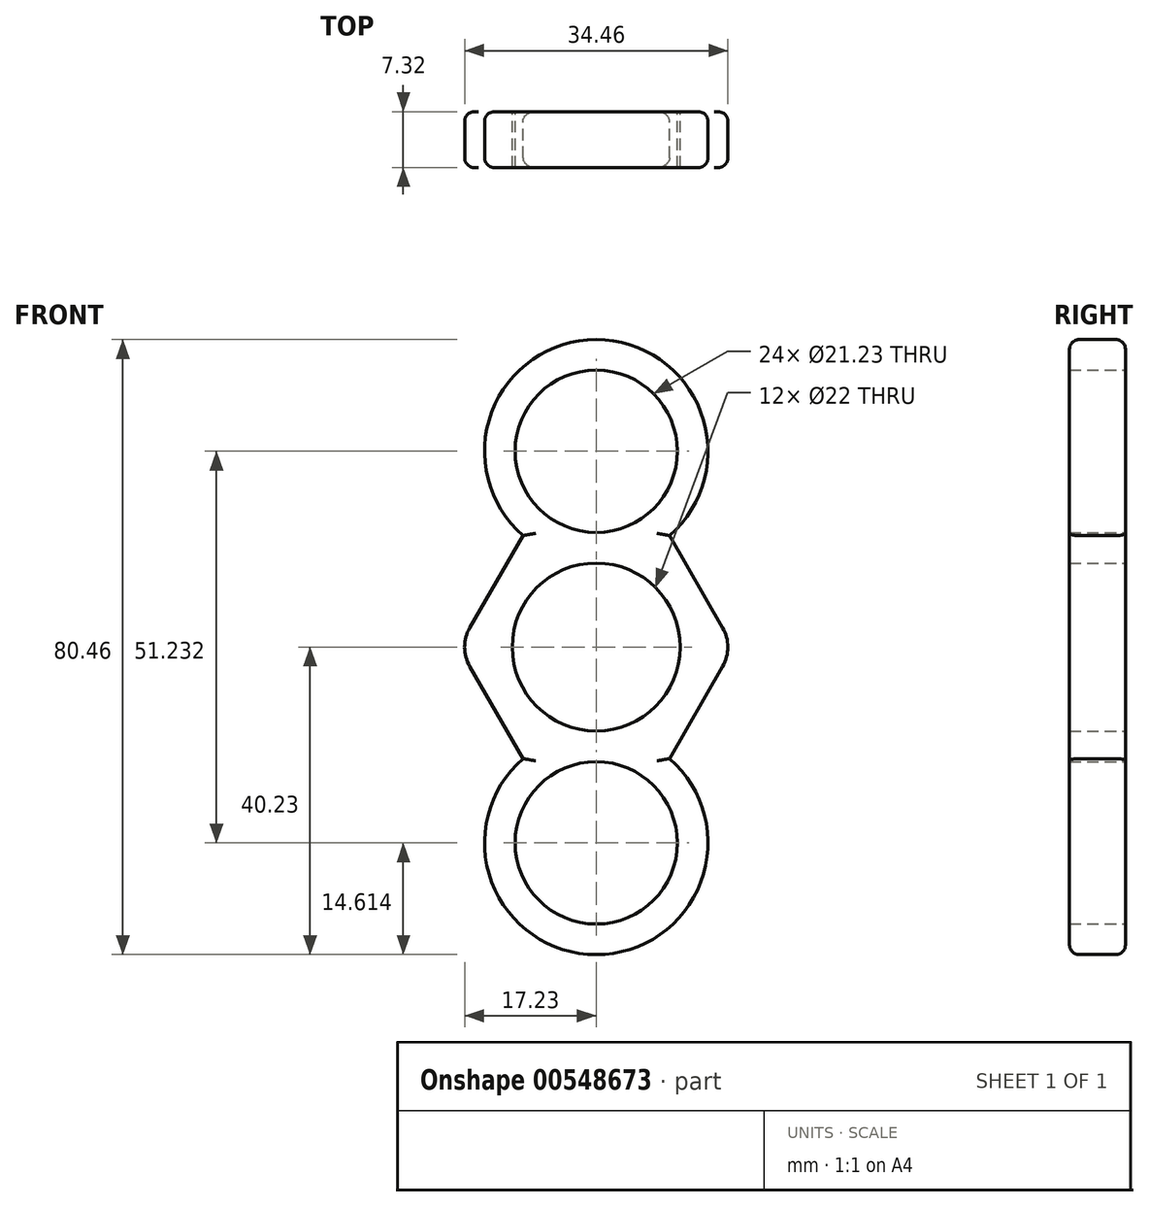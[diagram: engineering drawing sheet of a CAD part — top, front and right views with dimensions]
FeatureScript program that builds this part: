
annotation { "Feature Type Name" : "Feature", "Feature Type Description" : "" }
export const myFeature = defineFeature(function(context is Context, id is Id, definition is map)
    precondition{}
    {
        {
            var Q0;
            Q0=qCreatedBy(makeId("Front.planeOp"),FACE);
            var sketch = newSketch(context, id + "F0", { "sketchPlane" : qUnion([Q0])});
            skCircle(sketch, "E0", {"center": v(0, 0) * mm, "radius": 11 * mm});
            skCircle(sketch, "E1.cCircle", {"center": v(0, 0) * mm, "radius": 15.6 * mm, "construction": true});
            skLineSegment(sketch, "E1.0", {"start": v(-9, 15.6) * mm, "end": v(9, 15.6) * mm});
            skLineSegment(sketch, "E1.1", {"start": v(9, 15.6) * mm, "end": v(18.02, 0) * mm});
            skLineSegment(sketch, "E1.2", {"start": v(18.02, 0) * mm, "end": v(9, -15.6) * mm});
            skLineSegment(sketch, "E1.3", {"start": v(9, -15.6) * mm, "end": v(-9, -15.6) * mm});
            skLineSegment(sketch, "E1.4", {"start": v(-9, -15.6) * mm, "end": v(-18.02, 0) * mm});
            skLineSegment(sketch, "E1.5", {"start": v(-18.02, 0) * mm, "end": v(-9, 15.6) * mm});
            skPoint(sketch, "E1.0.midPoint", {"position": v(0, 15.6) * mm});
            skCircle(sketch, "E2", {"center": v(0, 25.62) * mm, "radius": 14.62 * mm});
            skCircle(sketch, "E3", {"center": v(0, 25.62) * mm, "radius": 10.62 * mm});
            skCircle(sketch, "E4.1.0", {"center": v(0, -25.62) * mm, "radius": 10.62 * mm});
            skCircle(sketch, "E4.1.1", {"center": v(0, -25.62) * mm, "radius": 14.62 * mm});
            skSolve(sketch);
        }
        {
            var Q0;
            Q0 = qSketchRegion(id + "F0", true);
            extrude(context, id + "F1", {"entities" : qUnion([Q0]), "depth" : 7.32 * mm, "offsetDistance" : 25.4 * mm});
        }
        {
            var Q0;
            Q0=makeQuery(id+"F1.opExtrude","CAP_EDGE",EDGE,{"disambiguationData":[OSD([sQuery(id+"F0.wireOp",EDGE,"E4.1.1")])],"isStart":false});
            var Q1;
            Q1=makeQuery(id+"F1.opExtrude","CAP_EDGE",EDGE,{"disambiguationData":[OSD([sQuery(id+"F0.wireOp",EDGE,"E2")])],"isStart":false});
            var Q2;
            Q2=makeQuery(id+"F1.opExtrude","CAP_EDGE",EDGE,{"disambiguationData":[OSD([sQuery(id+"F0.wireOp",EDGE,"E1.1")])],"isStart":false});
            var Q3;
            Q3=makeQuery(id+"F1.opExtrude","CAP_EDGE",EDGE,{"disambiguationData":[OSD([sQuery(id+"F0.wireOp",EDGE,"E1.2")])],"isStart":false});
            var Q4;
            Q4=makeQuery(id+"F1.opExtrude","CAP_EDGE",EDGE,{"disambiguationData":[OSD([sQuery(id+"F0.wireOp",EDGE,"E1.4")])],"isStart":false});
            var Q5;
            Q5=makeQuery(id+"F1.opExtrude","CAP_EDGE",EDGE,{"disambiguationData":[OSD([sQuery(id+"F0.wireOp",EDGE,"E1.5")])],"isStart":false});
            fillet(context, id + "F2", {"entities" : qUnion([Q0, Q1, Q2, Q3, Q4, Q5]), "radius" : 1.27 * mm, "tangentPropagation" : true, "allowEdgeOverflow" : false});
        }
        {
            var Q0;
            Q0=makeQuery(id+"F1.opExtrude","CAP_EDGE",EDGE,{"disambiguationData":[OSD([sQuery(id+"F0.wireOp",EDGE,"E4.1.1")])],"isStart":true});
            var Q1;
            Q1=makeQuery(id+"F1.opExtrude","CAP_EDGE",EDGE,{"disambiguationData":[OSD([sQuery(id+"F0.wireOp",EDGE,"E1.4")])],"isStart":true});
            var Q2;
            Q2=makeQuery(id+"F1.opExtrude","CAP_EDGE",EDGE,{"disambiguationData":[OSD([sQuery(id+"F0.wireOp",EDGE,"E1.5")])],"isStart":true});
            var Q3;
            Q3=makeQuery(id+"F1.opExtrude","CAP_EDGE",EDGE,{"disambiguationData":[OSD([sQuery(id+"F0.wireOp",EDGE,"E2")])],"isStart":true});
            var Q4;
            Q4=makeQuery(id+"F1.opExtrude","CAP_EDGE",EDGE,{"disambiguationData":[OSD([sQuery(id+"F0.wireOp",EDGE,"E1.1")])],"isStart":true});
            var Q5;
            Q5=makeQuery(id+"F1.opExtrude","CAP_EDGE",EDGE,{"disambiguationData":[OSD([sQuery(id+"F0.wireOp",EDGE,"E1.2")])],"isStart":true});
            fillet(context, id + "F3", {"entities" : qUnion([Q0, Q1, Q2, Q3, Q4, Q5]), "radius" : 1.27 * mm, "tangentPropagation" : true, "allowEdgeOverflow" : false});
        }
        {
            var Q0;
            Q0=makeQuery(id+"F1.opExtrude","SWEPT_EDGE",EDGE,{"disambiguationData":[OSD([sQuery(id+"F0.wireOp",EDGE,"E1.1"),sQuery(id+"F0.wireOp",EDGE,"E1.2")])]});
            var Q1;
            Q1=makeQuery(id+"F1.opExtrude","SWEPT_EDGE",EDGE,{"disambiguationData":[OSD([sQuery(id+"F0.wireOp",EDGE,"E1.4"),sQuery(id+"F0.wireOp",EDGE,"E1.5")])]});
            fillet(context, id + "F4", {"entities" : qUnion([Q0, Q1]), "radius" : 5.08 * mm, "tangentPropagation" : true, "allowEdgeOverflow" : false});
        }
    });
